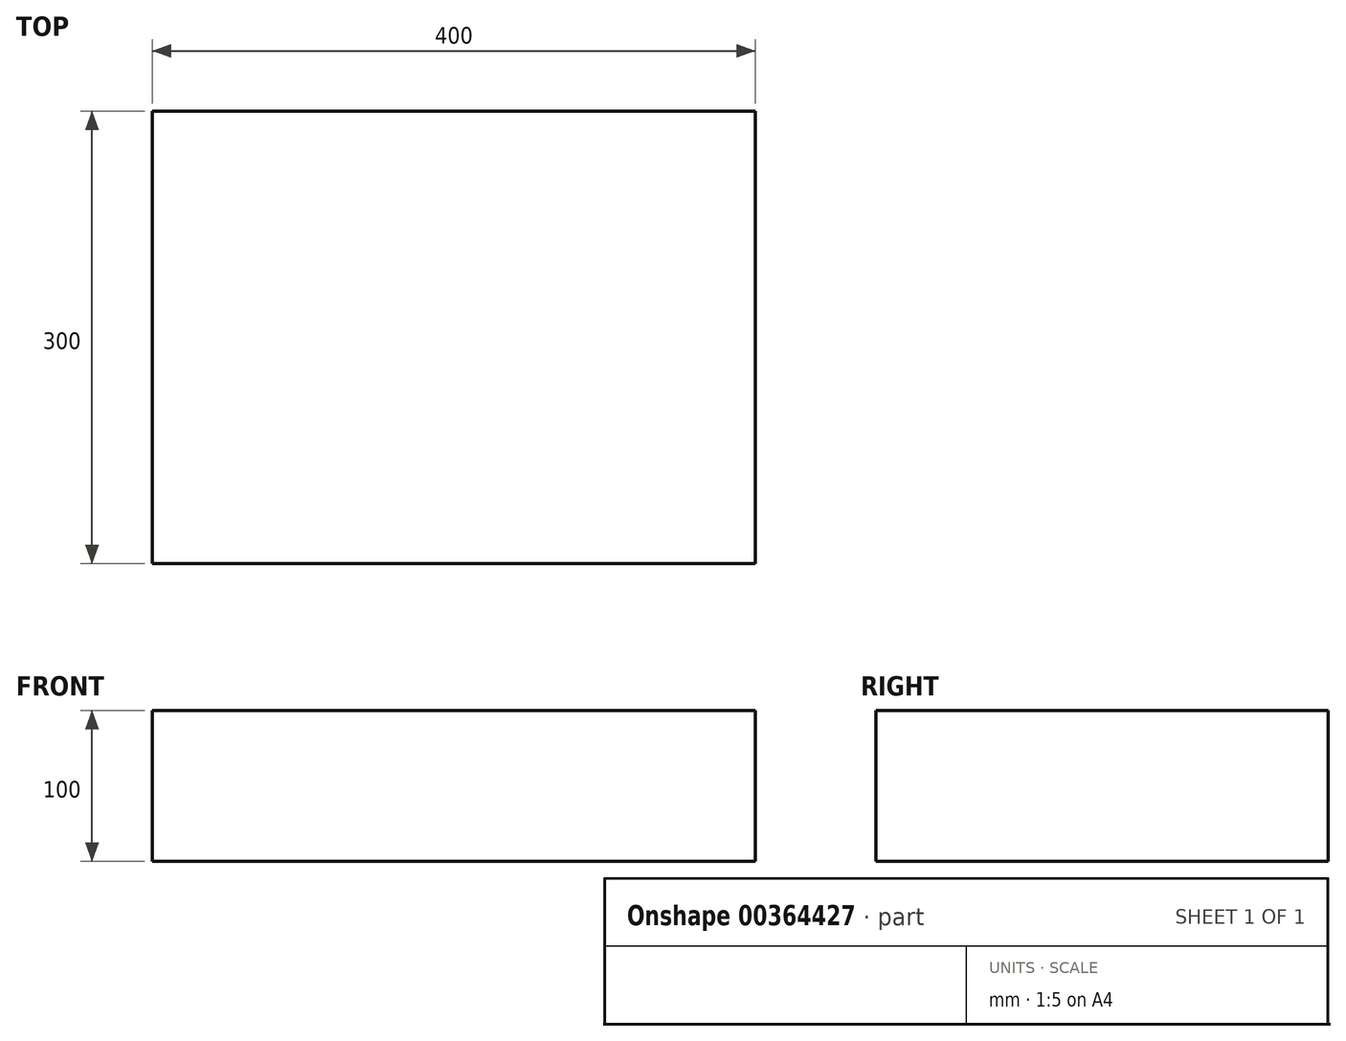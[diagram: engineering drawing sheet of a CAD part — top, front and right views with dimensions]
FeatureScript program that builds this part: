
annotation { "Feature Type Name" : "Feature", "Feature Type Description" : "" }
export const myFeature = defineFeature(function(context is Context, id is Id, definition is map)
    precondition{}
    {
        {
            var Q0;
            Q0=qCreatedBy(makeId("Top.planeOp"),FACE);
            var sketch = newSketch(context, id + "F0", { "sketchPlane" : qUnion([Q0])});
            skLineSegment(sketch, "E0.bottom", {"start": v(0, 0) * mm, "end": v(400, 0) * mm});
            skLineSegment(sketch, "E0.top", {"start": v(0, 300) * mm, "end": v(400, 300) * mm});
            skLineSegment(sketch, "E0.left", {"start": v(0, 0) * mm, "end": v(0, 300) * mm});
            skLineSegment(sketch, "E0.right", {"start": v(400, 0) * mm, "end": v(400, 300) * mm});
            skSolve(sketch);
        }
        {
            var Q0;
            Q0=makeQuery(id+"F0.imprint","IMPRINT",FACE,{"disambiguationData":[TD([[makeQuery(id+"F0.imprint","IMPRINT",EDGE,{"derivedFrom":sQuery(id+"F0.wireOp",EDGE,"E0.bottom")}),1.0]])]});
            extrude(context, id + "F1", {"entities" : qUnion([Q0]), "depth" : 100 * mm});
        }
    });
